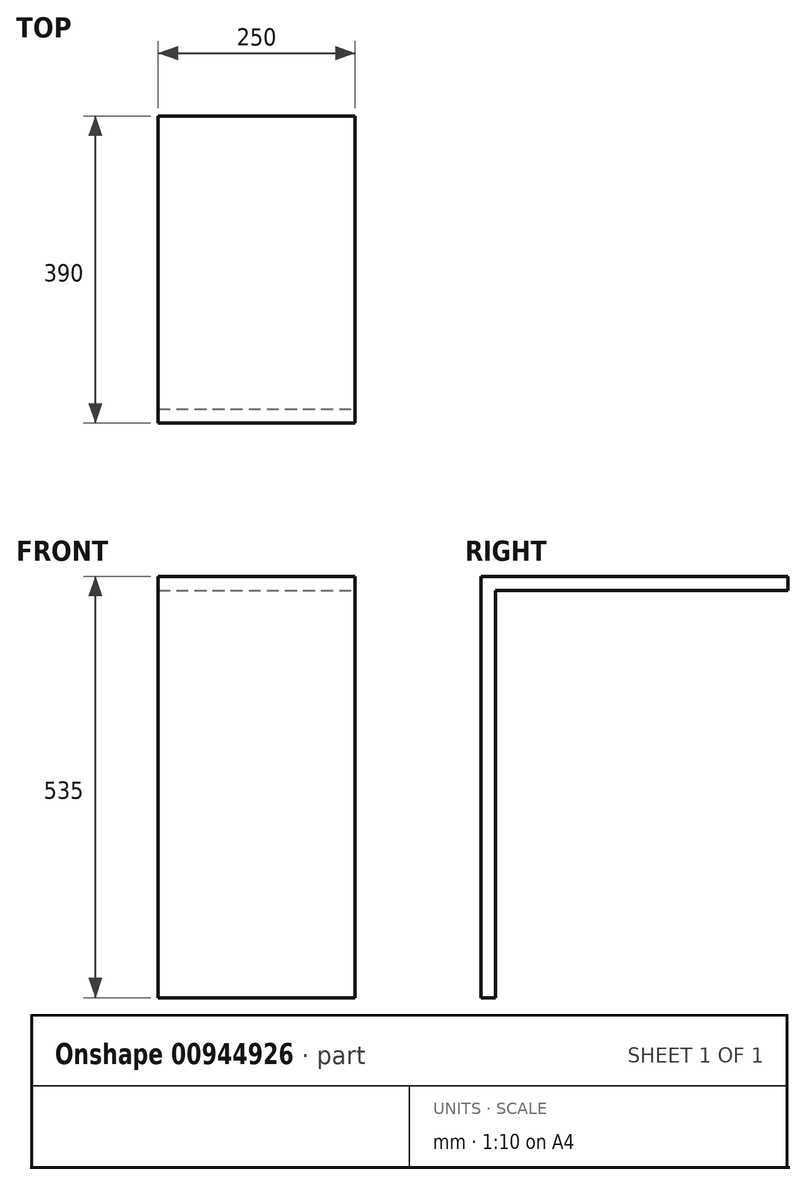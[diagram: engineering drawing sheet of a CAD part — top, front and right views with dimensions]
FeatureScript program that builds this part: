
annotation { "Feature Type Name" : "Feature", "Feature Type Description" : "" }
export const myFeature = defineFeature(function(context is Context, id is Id, definition is map)
    precondition{}
    {
        {
            var Q0;
            Q0=qCreatedBy(makeId("Front.planeOp"),FACE);
            var sketch = newSketch(context, id + "F0", { "sketchPlane" : qUnion([Q0])});
            skLineSegment(sketch, "E0.bottom", {"start": v(0, 0) * mm, "end": v(250, 0) * mm});
            skLineSegment(sketch, "E0.top", {"start": v(0, 517) * mm, "end": v(250, 517) * mm});
            skLineSegment(sketch, "E0.left", {"start": v(0, 0) * mm, "end": v(0, 517) * mm});
            skLineSegment(sketch, "E0.right", {"start": v(250, 0) * mm, "end": v(250, 517) * mm});
            skSolve(sketch);
        }
        {
            var Q0;
            Q0 = qSketchRegion(id + "F0", true);
            extrude(context, id + "F1", {"entities" : qUnion([Q0]), "depth" : 18 * mm, "offsetDistance" : 25 * mm});
        }
        {
            var Q0;
            Q0=makeQuery(id+"F1.opExtrude","CAP_FACE",FACE,{"disambiguationData":[OSD([sQuery(id+"F0.wireOp",EDGE,"E0.bottom"),sQuery(id+"F0.wireOp",EDGE,"E0.top"),sQuery(id+"F0.wireOp",EDGE,"E0.left"),sQuery(id+"F0.wireOp",EDGE,"E0.right")])],"isStart":false});
            var sketch = newSketch(context, id + "F2", { "sketchPlane" : qUnion([Q0])});
            skLineSegment(sketch, "E1.bottom", {"start": v(0, 517) * mm, "end": v(250, 517) * mm});
            skLineSegment(sketch, "E1.top", {"start": v(0, 535) * mm, "end": v(250, 535) * mm});
            skLineSegment(sketch, "E1.left", {"start": v(0, 517) * mm, "end": v(0, 535) * mm});
            skLineSegment(sketch, "E1.right", {"start": v(250, 517) * mm, "end": v(250, 535) * mm});
            skSolve(sketch);
        }
        {
            var Q0;
            Q0 = qSketchRegion(id + "F2", true);
            extrude(context, id + "F3", {"entities" : qUnion([Q0]), "operationType" : NewBodyOperationType.ADD, "oppositeDirection" : true, "depth" : 390 * mm, "offsetDistance" : 25 * mm});
        }
    });
